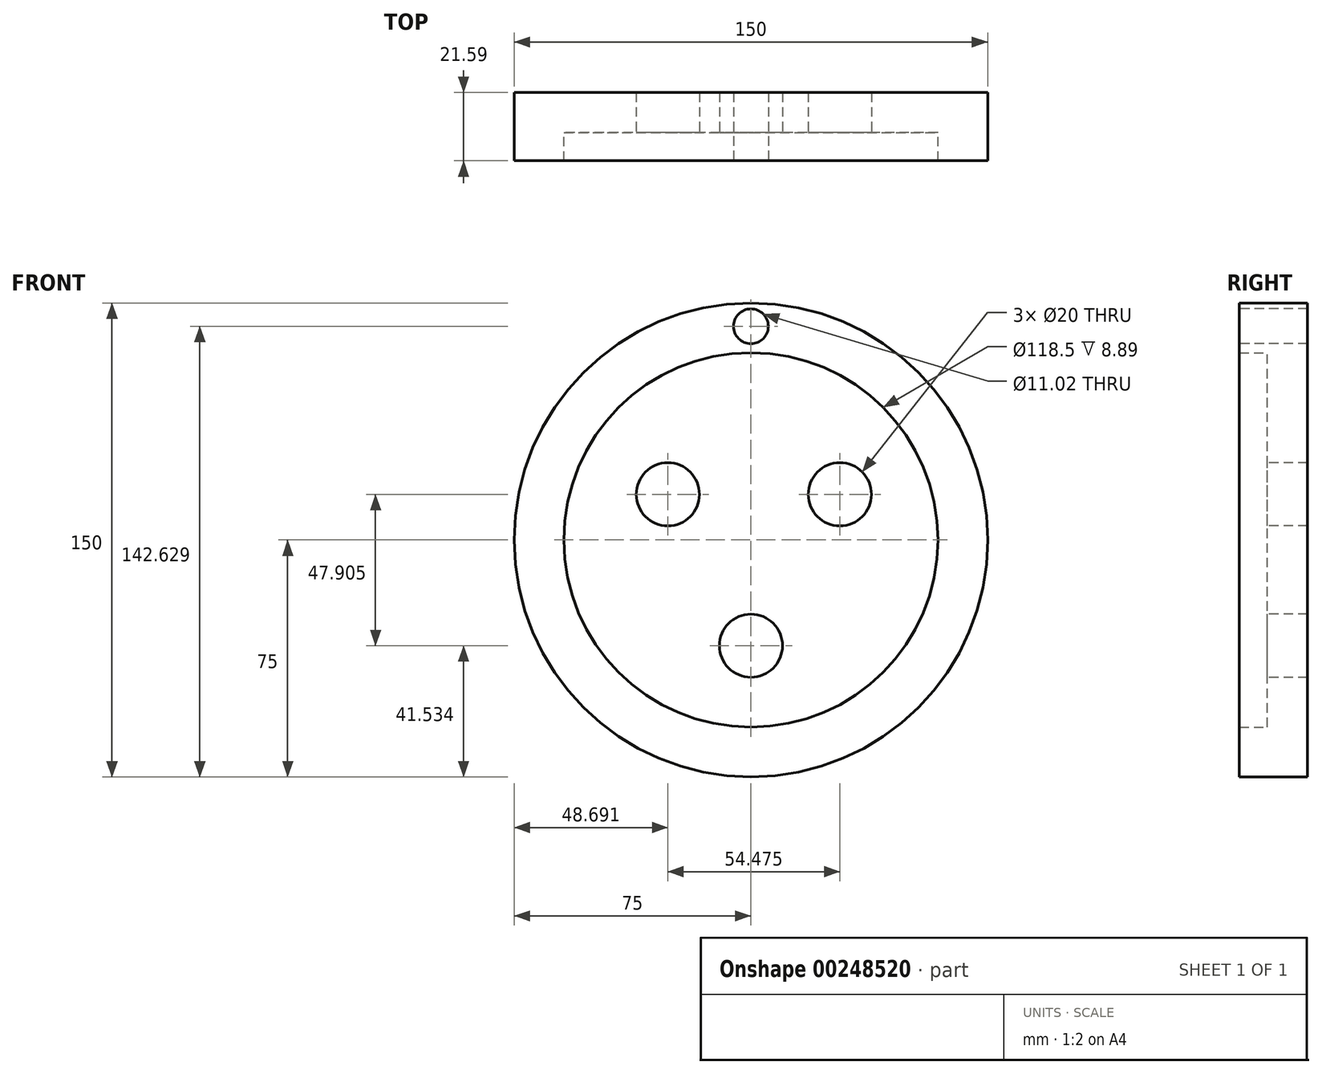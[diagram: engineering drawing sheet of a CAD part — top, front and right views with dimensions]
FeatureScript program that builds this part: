
annotation { "Feature Type Name" : "Feature", "Feature Type Description" : "" }
export const myFeature = defineFeature(function(context is Context, id is Id, definition is map)
    precondition{}
    {
        {
            var Q0;
            Q0=qCreatedBy(makeId("Front.planeOp"),FACE);
            var sketch = newSketch(context, id + "F0", { "sketchPlane" : qUnion([Q0])});
            skCircle(sketch, "E0", {"center": v(0, 0) * mm, "radius": 75 * mm});
            skSolve(sketch);
        }
        {
            var Q0;
            Q0=makeQuery(id+"F0.imprint","IMPRINT",FACE,{"disambiguationData":[TD([[makeQuery(id+"F0.imprint","IMPRINT",EDGE,{"derivedFrom":sQuery(id+"F0.wireOp",EDGE,"E0")}),1.0]])]});
            extrude(context, id + "F1", {"entities" : qUnion([Q0]), "depth" : 12.7 * mm});
        }
        {
            var Q0;
            Q0=makeQuery(id+"F1.opExtrude","CAP_FACE",FACE,{"disambiguationData":[OSD([sQuery(id+"F0.wireOp",EDGE,"E0")])],"isStart":false});
            var sketch = newSketch(context, id + "F2", { "sketchPlane" : qUnion([Q0])});
            skCircle(sketch, "E1.0", {"center": v(0, 0) * mm, "radius": 59.25 * mm});
            skSolve(sketch);
        }
        {
            var Q0;
            Q0=makeQuery(id+"F2.imprint","IMPRINT",FACE,{"disambiguationData":[TD([[makeQuery(id+"F2.imprint","IMPRINT",EDGE,{"derivedFrom":sQuery(id+"F2.wireOp",EDGE,"E1.0")}),-1.0]])]});
            extrude(context, id + "F3", {"entities" : qUnion([Q0]), "operationType" : NewBodyOperationType.ADD, "depth" : 8.9 * mm});
        }
        {
            var Q0;
            Q0=makeQuery(id+"F1.opExtrude","CAP_FACE",FACE,{"disambiguationData":[OSD([sQuery(id+"F0.wireOp",EDGE,"E0")])],"isStart":false});
            var sketch = newSketch(context, id + "F4", { "sketchPlane" : qUnion([Q0])});
            skLineSegment(sketch, "E2", {"start": v(-57.47, 14.44) * mm, "end": v(57.47, 14.44) * mm, "construction": true});
            skLineSegment(sketch, "E3", {"start": v(-48.9, -33.47) * mm, "end": v(48.9, -33.47) * mm, "construction": true});
            skCircle(sketch, "E4", {"center": v(-26.3, 14.44) * mm, "radius": 10 * mm});
            skCircle(sketch, "E5", {"center": v(28.17, 14.44) * mm, "radius": 10 * mm});
            skCircle(sketch, "E6", {"center": v(0, -33.47) * mm, "radius": 10 * mm});
            skSolve(sketch);
        }
        {
            var Q0;
            Q0 = qSketchRegion(id + "F4", true);
            extrude(context, id + "F5", {"entities" : qUnion([Q0]), "operationType" : NewBodyOperationType.REMOVE, "oppositeDirection" : true, "depth" : 25.4 * mm});
        }
        {
            var Q0;
            Q0=makeQuery(id+"F3.opExtrude","CAP_FACE",FACE,{"disambiguationData":[OSD([sQuery(id+"F0.wireOp",EDGE,"E0"),sQuery(id+"F2.wireOp",EDGE,"E1.0")])],"isStart":false});
            var sketch = newSketch(context, id + "F6", { "sketchPlane" : qUnion([Q0])});
            skCircle(sketch, "E7", {"center": v(0, 67.63) * mm, "radius": 5.51 * mm});
            skSolve(sketch);
        }
        {
            var Q0;
            Q0 = qSketchRegion(id + "F6", true);
            extrude(context, id + "F7", {"entities" : qUnion([Q0]), "operationType" : NewBodyOperationType.REMOVE, "oppositeDirection" : true, "depth" : 25.4 * mm});
        }
    });
